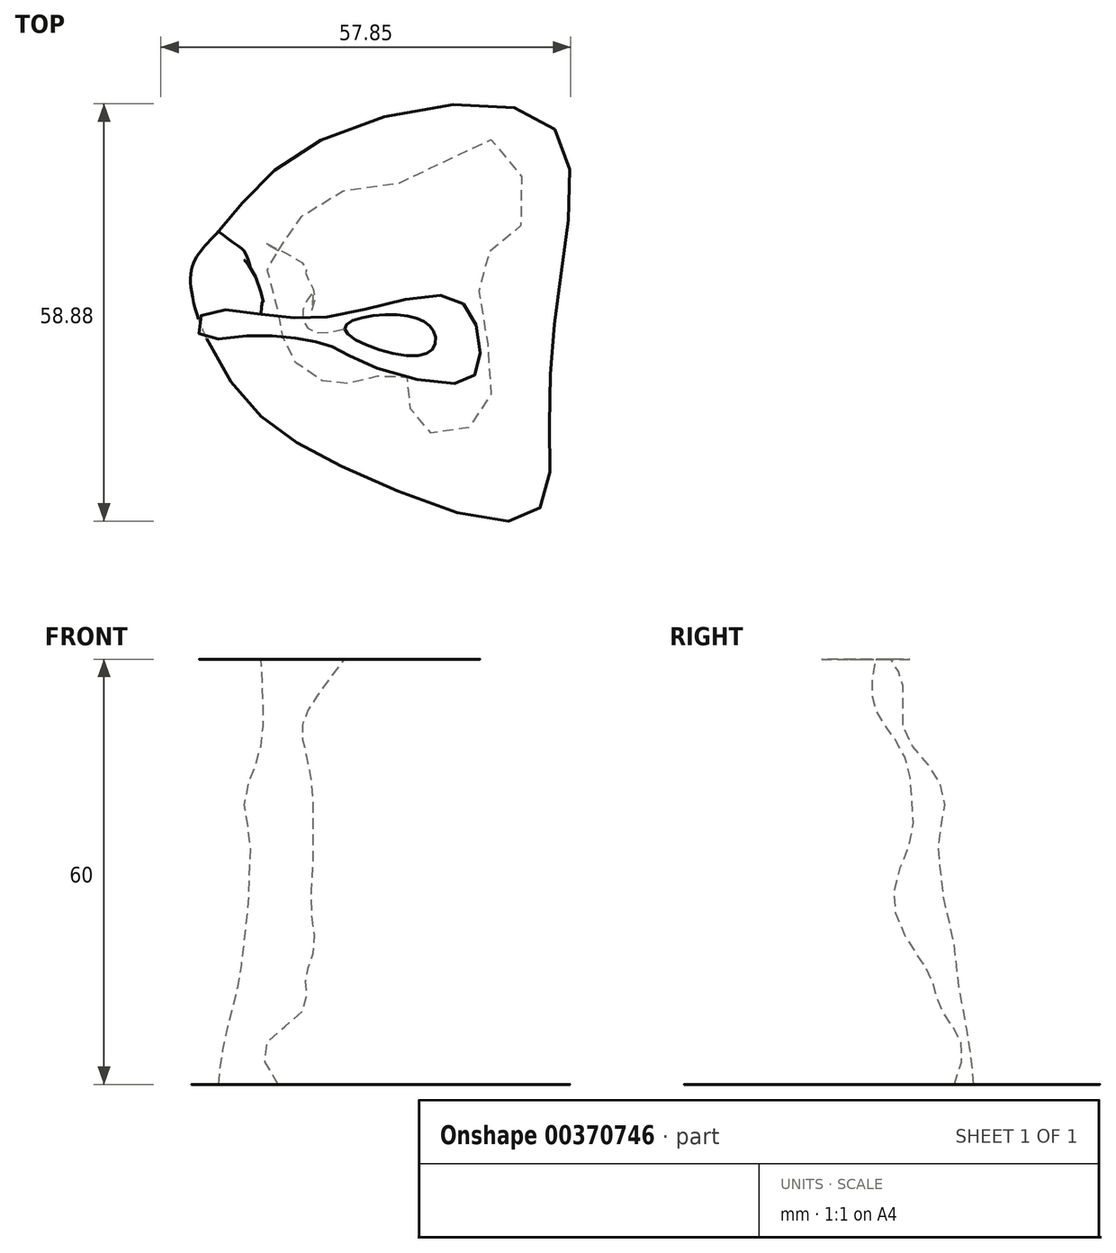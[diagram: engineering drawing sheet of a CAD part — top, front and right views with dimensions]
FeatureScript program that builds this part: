
annotation { "Feature Type Name" : "Feature", "Feature Type Description" : "" }
export const myFeature = defineFeature(function(context is Context, id is Id, definition is map)
    precondition{}
    {
        {
            var Q0;
            Q0=qCreatedBy(makeId("Top.planeOp"),FACE);
            cPlane(context, id + "F0", {"entities" : qUnion([Q0]), "cplaneType" : CPlaneType.OFFSET, "offset" : 5 * mm, "width" : 152.4 * mm, "height" : 152.4 * mm});
        }
        {
            var Q0;
            Q0=qCreatedBy(id+"F0.planeOp",FACE);
            var sketch = newSketch(context, id + "F1", { "sketchPlane" : qUnion([Q0])});
            skFitSpline(sketch, "E0", {"points": [v(-21.03, 11.8) * mm, v(-7.7, 24.1) * mm, v(25.13, 27.35) * mm, v(27.7, 8.72) * mm, v(25.64, -14.36) * mm, v(23.08, -28.38) * mm, v(-2.22, -22.05) * mm, v(-18.46, -10.6) * mm, v(-24.96, 5.81) * mm, v(-21.03, 11.8) * mm]});
            skSolve(sketch);
        }
        {
            var Q0;
            Q0=qCreatedBy(id+"F0.planeOp",FACE);
            var sketch = newSketch(context, id + "F2", { "sketchPlane" : qUnion([Q0])});
            skFitSpline(sketch, "E1", {"points": [v(-12.65, 9.06) * mm, v(-6.84, 16.24) * mm, v(7.86, 19.66) * mm, v(17.78, 24.62) * mm, v(22.22, 13.85) * mm, v(16.58, 8.2) * mm, v(16.58, -2.4) * mm, v(16.58, -13.68) * mm, v(10.09, -16.93) * mm, v(6.15, -13.85) * mm, v(5.64, -8.9) * mm, v(1.2, -8.72) * mm, v(-3.08, -9.74) * mm, v(-6.15, -9.4) * mm, v(-10.26, -6.67) * mm, v(-11.97, -3.08) * mm, v(-12.48, 0) * mm, v(-14.19, 7.35) * mm, v(-12.65, 9.06) * mm]});
            skSolve(sketch);
        }
        {
            var Q0;
            Q0=qCreatedBy(id+"F0.planeOp",FACE);
            cPlane(context, id + "F3", {"entities" : qUnion([Q0]), "cplaneType" : CPlaneType.OFFSET, "offset" : 5 * mm, "width" : 152.4 * mm, "height" : 152.4 * mm});
        }
        {
            var Q0;
            Q0=qCreatedBy(id+"F3.planeOp",FACE);
            var sketch = newSketch(context, id + "F4", { "sketchPlane" : qUnion([Q0])});
            skFitSpline(sketch, "E2", {"points": [v(-14.87, 16.93) * mm, v(-6.84, 23.6) * mm, v(6.5, 27.7) * mm, v(22.05, 28.38) * mm, v(27.18, 22.9) * mm, v(27.52, 18.12) * mm, v(25.13, 12.3) * mm, v(23.25, 8.04) * mm, v(21.88, 2.9) * mm, v(21.03, -3.25) * mm, v(22.05, -8.2) * mm, v(24.1, -13.34) * mm, v(25.13, -17.95) * mm, v(24.45, -24.1) * mm, v(21.88, -27.52) * mm, v(17.44, -27.87) * mm, v(9.57, -26.16) * mm, v(2.05, -22.9) * mm, v(-9.06, -17.27) * mm, v(-20.34, -6.5) * mm, v(-24.28, 3.76) * mm, v(-20.69, 10.94) * mm, v(-14.87, 16.93) * mm]});
            skSolve(sketch);
        }
        {
            var Q0;
            Q0=qCreatedBy(id+"F3.planeOp",FACE);
            var sketch = newSketch(context, id + "F5", { "sketchPlane" : qUnion([Q0])});
            skFitSpline(sketch, "E3", {"points": [v(-15.22, 0) * mm, v(-15.9, 7) * mm, v(-12.65, 12.82) * mm, v(-5.81, 15.56) * mm, v(9.74, 16.24) * mm, v(15.73, 20) * mm, v(17.78, 15.9) * mm, v(15.39, 10.77) * mm, v(14.87, 5.13) * mm, v(14.87, 0) * mm, v(15.39, -7) * mm, v(16.07, -12.65) * mm, v(15.73, -17.6) * mm, v(8.55, -19.66) * mm, v(5.47, -16.93) * mm, v(4.27, -13) * mm, v(1.2, -11.11) * mm, v(-5.3, -11.11) * mm, v(-11.28, -9.23) * mm, v(-12.65, -6.5) * mm, v(-15.22, 0) * mm]});
            skSolve(sketch);
        }
        {
            var Q0;
            Q0=qCreatedBy(id+"F3.planeOp",FACE);
            cPlane(context, id + "F6", {"entities" : qUnion([Q0]), "cplaneType" : CPlaneType.OFFSET, "offset" : 5 * mm, "width" : 152.4 * mm, "height" : 152.4 * mm});
        }
        {
            var Q0;
            Q0=qCreatedBy(id+"F6.planeOp",FACE);
            var sketch = newSketch(context, id + "F7", { "sketchPlane" : qUnion([Q0])});
            skFitSpline(sketch, "E4", {"points": [v(-22.9, 3.25) * mm, v(-18.98, 10.77) * mm, v(-12.82, 16.93) * mm, v(-2.56, 24.28) * mm, v(12.14, 27.35) * mm, v(22.05, 27.7) * mm, v(26.67, 21.54) * mm, v(25.3, 15.04) * mm, v(17.6, 8.38) * mm, v(15.73, 4.27) * mm, v(15.73, -3.25) * mm, v(18.12, -8.9) * mm, v(20.52, -11.8) * mm, v(21.88, -17.27) * mm, v(20.52, -21.03) * mm, v(14.7, -22.4) * mm, v(4.1, -20.69) * mm, v(-4.1, -18.12) * mm, v(-12.3, -15.04) * mm, v(-17.95, -9.06) * mm, v(-23.6, -4.79) * mm, v(-22.9, 3.25) * mm]});
            skSolve(sketch);
        }
        {
            var Q0;
            Q0=qCreatedBy(id+"F6.planeOp",FACE);
            var sketch = newSketch(context, id + "F8", { "sketchPlane" : qUnion([Q0])});
            skFitSpline(sketch, "E5", {"points": [v(-9.74, 6.84) * mm, v(-4.27, 11.28) * mm, v(6.67, 15.04) * mm, v(10.43, 12.48) * mm, v(10.26, 6.33) * mm, v(9.06, 1.88) * mm, v(8.72, -5.47) * mm, v(7.7, -8.9) * mm, v(4.96, -9.23) * mm, v(-3.93, -8.72) * mm, v(-5.81, -7) * mm, v(-7.35, -3.42) * mm, v(-8.72, 0) * mm, v(-9.74, 6.84) * mm]});
            skSolve(sketch);
        }
        {
            var Q0;
            Q0=qCreatedBy(id+"F6.planeOp",FACE);
            cPlane(context, id + "F9", {"entities" : qUnion([Q0]), "cplaneType" : CPlaneType.OFFSET, "offset" : 5 * mm, "width" : 152.4 * mm, "height" : 152.4 * mm});
        }
        {
            var Q0;
            Q0=qCreatedBy(id+"F9.planeOp",FACE);
            var sketch = newSketch(context, id + "F10", { "sketchPlane" : qUnion([Q0])});
            skFitSpline(sketch, "E6", {"points": [v(-20.34, 7) * mm, v(-13.68, 15.73) * mm, v(-5.64, 22.23) * mm, v(7.7, 26.33) * mm, v(20.86, 27.87) * mm, v(24.96, 25.47) * mm, v(26.5, 19.15) * mm, v(22.74, 14.36) * mm, v(13.16, 9.74) * mm, v(8.55, 3.08) * mm, v(10.94, -3.76) * mm, v(15.9, -9.92) * mm, v(16.75, -14.87) * mm, v(12.48, -17.44) * mm, v(3.25, -17.95) * mm, v(-6.84, -17.1) * mm, v(-14.36, -16.75) * mm, v(-22.74, -14.02) * mm, v(-27.87, -4.27) * mm, v(-24.62, 4.27) * mm, v(-20.34, 7) * mm]});
            skSolve(sketch);
        }
        {
            var Q0;
            Q0=qCreatedBy(id+"F9.planeOp",FACE);
            var sketch = newSketch(context, id + "F11", { "sketchPlane" : qUnion([Q0])});
            skFitSpline(sketch, "E7", {"points": [v(-7, 6.67) * mm, v(-4.27, 8.55) * mm, v(0, 8.9) * mm, v(2.4, 5.64) * mm, v(2.9, 0) * mm, v(2.74, -3.08) * mm, v(2.22, -8.38) * mm, v(-2.22, -9.92) * mm, v(-9.23, -9.57) * mm, v(-14.19, -8.2) * mm, v(-18.63, 0) * mm, v(-15.39, 3.42) * mm, v(-10.94, 4.96) * mm, v(-7, 6.67) * mm]});
            skSolve(sketch);
        }
        {
            var Q0;
            Q0=qCreatedBy(id+"F9.planeOp",FACE);
            cPlane(context, id + "F12", {"entities" : qUnion([Q0]), "cplaneType" : CPlaneType.OFFSET, "offset" : 5 * mm, "width" : 152.4 * mm, "height" : 152.4 * mm});
        }
        {
            var Q0;
            Q0=qCreatedBy(id+"F12.planeOp",FACE);
            var sketch = newSketch(context, id + "F13", { "sketchPlane" : qUnion([Q0])});
            skFitSpline(sketch, "E8", {"points": [v(-21.2, 5.98) * mm, v(-14.7, 12.48) * mm, v(-6.84, 20.52) * mm, v(7.18, 25.13) * mm, v(20.69, 27.35) * mm, v(26.16, 23.08) * mm, v(24.62, 17.78) * mm, v(13, 13.16) * mm, v(5.13, 8.2) * mm, v(3.6, 0) * mm, v(5.81, -3.42) * mm, v(10.6, -8.04) * mm, v(13.34, -13.16) * mm, v(3.08, -15.56) * mm, v(-17.44, -15.56) * mm, v(-25.3, -14.36) * mm, v(-28.2, -9.4) * mm, v(-28.72, -1.7) * mm, v(-25.47, 5.3) * mm, v(-21.2, 5.98) * mm]});
            skSolve(sketch);
        }
        {
            var Q0;
            Q0=qCreatedBy(id+"F12.planeOp",FACE);
            var sketch = newSketch(context, id + "F14", { "sketchPlane" : qUnion([Q0])});
            skFitSpline(sketch, "E9", {"points": [v(-16.07, 0) * mm, v(-9.57, 1.7) * mm, v(-5.3, 2.9) * mm, v(-2.9, -1.7) * mm, v(-2.9, -5.64) * mm, v(-9.74, -8.38) * mm, v(-16.93, -8.2) * mm, v(-20.52, -4.96) * mm, v(-18.46, 0) * mm, v(-16.07, 0) * mm]});
            skSolve(sketch);
        }
        {
            var Q0;
            Q0=qCreatedBy(id+"F12.planeOp",FACE);
            cPlane(context, id + "F15", {"entities" : qUnion([Q0]), "cplaneType" : CPlaneType.OFFSET, "offset" : 5 * mm, "width" : 152.4 * mm, "height" : 152.4 * mm});
        }
        {
            var Q0;
            Q0=qCreatedBy(id+"F15.planeOp",FACE);
            var sketch = newSketch(context, id + "F16", { "sketchPlane" : qUnion([Q0])});
            skFitSpline(sketch, "E10", {"points": [v(-13.5, 9.92) * mm, v(-9.74, 14.19) * mm, v(0, 20.34) * mm, v(8.55, 21.88) * mm, v(18.12, 21.88) * mm, v(19.66, 19.83) * mm, v(16.58, 18.12) * mm, v(9.23, 17.27) * mm, v(4.1, 15.22) * mm, v(2.22, 5.64) * mm, v(1.88, -1.7) * mm, v(4.27, -5.98) * mm, v(5.64, -9.57) * mm, v(2.4, -12.48) * mm, v(-7, -14.7) * mm, v(-18.8, -14.87) * mm, v(-24.28, -9.92) * mm, v(-25.47, 0) * mm, v(-22.22, 4.79) * mm, v(-16.41, 8.04) * mm, v(-13.5, 9.92) * mm]});
            skSolve(sketch);
        }
        {
            var Q0;
            Q0=qCreatedBy(id+"F15.planeOp",FACE);
            var sketch = newSketch(context, id + "F17", { "sketchPlane" : qUnion([Q0])});
            skFitSpline(sketch, "E11", {"points": [v(-16.07, -1.88) * mm, v(-12.65, 0) * mm, v(-6.84, 0) * mm, v(-6.5, -4.79) * mm, v(-10.26, -6.5) * mm, v(-14.7, -6.5) * mm, v(-16.93, -3.42) * mm, v(-16.07, -1.88) * mm]});
            skSolve(sketch);
        }
        {
            var Q0;
            Q0=qCreatedBy(id+"F15.planeOp",FACE);
            cPlane(context, id + "F18", {"entities" : qUnion([Q0]), "cplaneType" : CPlaneType.OFFSET, "offset" : 5 * mm, "width" : 152.4 * mm, "height" : 152.4 * mm});
        }
        {
            var Q0;
            Q0=qCreatedBy(id+"F18.planeOp",FACE);
            var sketch = newSketch(context, id + "F19", { "sketchPlane" : qUnion([Q0])});
            skFitSpline(sketch, "E12", {"points": [v(-11.97, 9.06) * mm, v(-6.67, 13.5) * mm, v(0, 18.3) * mm, v(3.42, 17.1) * mm, v(4.96, 13.34) * mm, v(5.98, 3.42) * mm, v(4.96, -3.42) * mm, v(3.76, -9.92) * mm, v(0, -11.97) * mm, v(-10.43, -13.85) * mm, v(-19.83, -14.02) * mm, v(-25.3, -11.28) * mm, v(-27.01, -3.25) * mm, v(-24.62, 3.93) * mm, v(-17.1, 7) * mm, v(-11.97, 9.06) * mm]});
            skSolve(sketch);
        }
        {
            var Q0;
            Q0=qCreatedBy(id+"F18.planeOp",FACE);
            var sketch = newSketch(context, id + "F20", { "sketchPlane" : qUnion([Q0])});
            skFitSpline(sketch, "E13", {"points": [v(-13.16, -4.62) * mm, v(-19.32, -3.6) * mm, v(-17.78, 0) * mm, v(-10.09, 1.54) * mm, v(-6.33, 0) * mm, v(-6.67, -5.64) * mm, v(-13.16, -4.62) * mm]});
            skSolve(sketch);
        }
        {
            var Q0;
            Q0=qCreatedBy(id+"F18.planeOp",FACE);
            cPlane(context, id + "F21", {"entities" : qUnion([Q0]), "cplaneType" : CPlaneType.OFFSET, "offset" : 5 * mm, "width" : 152.4 * mm, "height" : 152.4 * mm});
        }
        {
            var Q0;
            Q0=qCreatedBy(id+"F21.planeOp",FACE);
            var sketch = newSketch(context, id + "F22", { "sketchPlane" : qUnion([Q0])});
            skFitSpline(sketch, "E14", {"points": [v(-10.43, 7.7) * mm, v(-4.27, 13.5) * mm, v(3.08, 18.46) * mm, v(12.14, 18.63) * mm, v(13.85, 13.68) * mm, v(12.3, 9.4) * mm, v(11.11, 4.62) * mm, v(11.28, -1.37) * mm, v(9.74, -7.35) * mm, v(10.43, -13.68) * mm, v(6.5, -17.44) * mm, v(0, -18.63) * mm, v(-10.6, -19.32) * mm, v(-22.22, -13) * mm, v(-26.33, -2.22) * mm, v(-24.96, 3.08) * mm, v(-18.63, 6.67) * mm, v(-10.43, 7.7) * mm]});
            skSolve(sketch);
        }
        {
            var Q0;
            Q0=qCreatedBy(id+"F21.planeOp",FACE);
            var sketch = newSketch(context, id + "F23", { "sketchPlane" : qUnion([Q0])});
            skFitSpline(sketch, "E15", {"points": [v(-16.07, 0) * mm, v(-14.36, 1.88) * mm, v(-5.98, 2.74) * mm, v(-5.13, 0) * mm, v(-7.35, -5.81) * mm, v(-13, -6.84) * mm, v(-16.07, 0) * mm]});
            skSolve(sketch);
        }
        {
            var Q0;
            Q0=qCreatedBy(id+"F21.planeOp",FACE);
            cPlane(context, id + "F24", {"entities" : qUnion([Q0]), "cplaneType" : CPlaneType.OFFSET, "offset" : 5 * mm, "width" : 152.4 * mm, "height" : 152.4 * mm});
        }
        {
            var Q0;
            Q0=qCreatedBy(id+"F24.planeOp",FACE);
            var sketch = newSketch(context, id + "F25", { "sketchPlane" : qUnion([Q0])});
            skFitSpline(sketch, "E16", {"points": [v(-16.75, 8.2) * mm, v(-6.84, 13.85) * mm, v(0, 19.15) * mm, v(17.27, 20.69) * mm, v(21.2, 14.36) * mm, v(21.71, 6.5) * mm, v(21.37, 0) * mm, v(13.85, -13) * mm, v(3.42, -16.24) * mm, v(-12.82, -14.53) * mm, v(-24.45, -10.94) * mm, v(-27.18, 1.54) * mm, v(-19.49, 5.98) * mm, v(-16.75, 8.2) * mm]});
            skSolve(sketch);
        }
        {
            var Q0;
            Q0=qCreatedBy(id+"F24.planeOp",FACE);
            var sketch = newSketch(context, id + "F26", { "sketchPlane" : qUnion([Q0])});
            skFitSpline(sketch, "E17", {"points": [v(-10.94, -3.6) * mm, v(-19.83, -1.7) * mm, v(-17.78, 3.42) * mm, v(-8.38, 3.6) * mm, v(-5.13, -1.88) * mm, v(-10.94, -3.6) * mm]});
            skSolve(sketch);
        }
        {
            var Q0;
            Q0=qCreatedBy(id+"F24.planeOp",FACE);
            cPlane(context, id + "F27", {"entities" : qUnion([Q0]), "cplaneType" : CPlaneType.OFFSET, "offset" : 5 * mm, "width" : 152.4 * mm, "height" : 152.4 * mm});
        }
        {
            var Q0;
            Q0=qCreatedBy(id+"F27.planeOp",FACE);
            var sketch = newSketch(context, id + "F28", { "sketchPlane" : qUnion([Q0])});
            skFitSpline(sketch, "E18", {"points": [v(-22.22, 1.54) * mm, v(-14.19, 6.5) * mm, v(-9.92, 8.72) * mm, v(-3.42, 13.34) * mm, v(5.3, 15.56) * mm, v(13.85, 16.58) * mm, v(20.52, 13) * mm, v(24.1, 4.1) * mm, v(23.6, -4.27) * mm, v(22.9, -9.06) * mm, v(19.49, -14.53) * mm, v(15.22, -16.07) * mm, v(5.98, -16.07) * mm, v(-4.1, -13.5) * mm, v(-8.2, -11.97) * mm, v(-16.24, -10.43) * mm, v(-21.71, -9.57) * mm, v(-24.45, -8.72) * mm, v(-27.35, -6.84) * mm, v(-26.16, 0) * mm, v(-22.22, 1.54) * mm]});
            skSolve(sketch);
        }
        {
            var Q0;
            Q0=qCreatedBy(id+"F27.planeOp",FACE);
            var sketch = newSketch(context, id + "F29", { "sketchPlane" : qUnion([Q0])});
            skFitSpline(sketch, "E19", {"points": [v(-17.27, 0) * mm, v(-10.26, 3.42) * mm, v(-6.67, 0) * mm, v(-4.27, -5.98) * mm, v(-10.26, -4.45) * mm, v(-14.36, -4.27) * mm, v(-17.27, 0) * mm]});
            skSolve(sketch);
        }
        {
            var Q0;
            Q0=qCreatedBy(id+"F27.planeOp",FACE);
            cPlane(context, id + "F30", {"entities" : qUnion([Q0]), "cplaneType" : CPlaneType.OFFSET, "offset" : 5 * mm, "width" : 152.4 * mm, "height" : 152.4 * mm});
        }
        {
            var Q0;
            Q0=qCreatedBy(id+"F30.planeOp",FACE);
            var sketch = newSketch(context, id + "F31", { "sketchPlane" : qUnion([Q0])});
            skFitSpline(sketch, "E20", {"points": [v(-18.63, 1.54) * mm, v(-14.87, 1.88) * mm, v(-8.04, 5.13) * mm, v(-1.88, 8.55) * mm, v(4.96, 11.63) * mm, v(10.94, 11.63) * mm, v(22.4, 7.52) * mm, v(23.42, 3.25) * mm, v(25.13, -9.06) * mm, v(23.42, -15.04) * mm, v(19.32, -18.12) * mm, v(13.68, -19.66) * mm, v(9.4, -19.32) * mm, v(4.96, -17.27) * mm, v(2.9, -13.85) * mm, v(-3.93, -10.77) * mm, v(-6.5, -9.92) * mm, v(-10.26, -8.72) * mm, v(-14.87, -8.04) * mm, v(-17.44, -8.2) * mm, v(-21.54, -8.9) * mm, v(-28.04, -7.52) * mm, v(-27.52, -4.27) * mm, v(-25.3, 0) * mm, v(-18.63, 1.54) * mm]});
            skSolve(sketch);
        }
        {
            var Q0;
            Q0=qCreatedBy(id+"F30.planeOp",FACE);
            var sketch = newSketch(context, id + "F32", { "sketchPlane" : qUnion([Q0])});
            skFitSpline(sketch, "E21", {"points": [v(-16.75, -1.37) * mm, v(-10.43, 0) * mm, v(-5.98, -1.88) * mm, v(2.05, -3.25) * mm, v(6.84, -8.04) * mm, v(1.37, -7.7) * mm, v(-4.79, -4.27) * mm, v(-12.3, -2.22) * mm, v(-16.75, -1.37) * mm]});
            skSolve(sketch);
        }
        {
            var Q0;
            Q0=qCreatedBy(id+"F30.planeOp",FACE);
            cPlane(context, id + "F33", {"entities" : qUnion([Q0]), "cplaneType" : CPlaneType.OFFSET, "offset" : 5 * mm, "width" : 152.4 * mm, "height" : 152.4 * mm});
        }
        {
            var Q0;
            Q0=qCreatedBy(id+"F33.planeOp",FACE);
            var sketch = newSketch(context, id + "F34", { "sketchPlane" : qUnion([Q0])});
            skFitSpline(sketch, "E22", {"points": [v(-25.64, 0) * mm, v(-5.3, 3.6) * mm, v(1.37, 8.04) * mm, v(12.65, 9.23) * mm, v(19.83, 7) * mm, v(22.9, 0) * mm, v(24.79, -14.87) * mm, v(22.4, -22.9) * mm, v(11.8, -24.79) * mm, v(9.23, -23.76) * mm, v(5.64, -20.17) * mm, v(-2.05, -8.55) * mm, v(-12.14, -6.84) * mm, v(-23.6, -6.5) * mm, v(-26.84, -2.9) * mm, v(-25.64, 0) * mm]});
            skSolve(sketch);
        }
        {
            var Q0;
            Q0=qCreatedBy(id+"F33.planeOp",FACE);
            var sketch = newSketch(context, id + "F35", { "sketchPlane" : qUnion([Q0])});
            skFitSpline(sketch, "E23", {"points": [v(-5.3, -1.54) * mm, v(6.33, -2.56) * mm, v(11.11, -4.79) * mm, v(13.5, -9.57) * mm, v(6.84, -9.74) * mm, v(0, -6.5) * mm, v(-7.52, -4.27) * mm, v(-5.3, -1.54) * mm]});
            skSolve(sketch);
        }
        {
            var Q0;
            Q0=qCreatedBy(id+"F33.planeOp",FACE);
            cPlane(context, id + "F36", {"entities" : qUnion([Q0]), "cplaneType" : CPlaneType.OFFSET, "offset" : 5 * mm, "width" : 152.4 * mm, "height" : 152.4 * mm});
        }
        {
            var Q0;
            Q0=qCreatedBy(id+"F36.planeOp",FACE);
            var sketch = newSketch(context, id + "F37", { "sketchPlane" : qUnion([Q0])});
            skFitSpline(sketch, "E24", {"points": [v(-23.42, 0) * mm, v(-14.53, 0) * mm, v(-3.76, 0) * mm, v(10.26, 2.74) * mm, v(14.7, 0) * mm, v(15.73, -6.84) * mm, v(13.34, -9.57) * mm, v(0, -7) * mm, v(-4.79, -4.62) * mm, v(-7.52, -3.76) * mm, v(-11.8, -3.08) * mm, v(-17.95, -3.08) * mm, v(-23.6, -2.9) * mm, v(-23.42, 0) * mm]});
            skSolve(sketch);
        }
        {
            var Q0;
            Q0=qCreatedBy(id+"F36.planeOp",FACE);
            var sketch = newSketch(context, id + "F38", { "sketchPlane" : qUnion([Q0])});
            skFitSpline(sketch, "E25", {"points": [v(-3.25, -2.05) * mm, v(4.27, 0) * mm, v(9.4, -2.56) * mm, v(7.86, -5.64) * mm, v(-3.25, -2.05) * mm]});
            skSolve(sketch);
        }
        {
            var Q0;
            Q0 = qSketchRegion(id + "F1", true);
            var Q1;
            Q1 = qSketchRegion(id + "F4", true);
            var Q2;
            Q2 = qSketchRegion(id + "F7", true);
            var Q3;
            Q3 = qSketchRegion(id + "F10", true);
            var Q4;
            Q4 = qSketchRegion(id + "F13", true);
            var Q5;
            Q5 = qSketchRegion(id + "F16", true);
            var Q6;
            Q6 = qSketchRegion(id + "F19", true);
            var Q7;
            Q7 = qSketchRegion(id + "F22", true);
            var Q8;
            Q8 = qSketchRegion(id + "F25", true);
            var Q9;
            Q9 = qSketchRegion(id + "F28", true);
            var Q10;
            Q10 = qSketchRegion(id + "F31", true);
            var Q11;
            Q11 = qSketchRegion(id + "F34", true);
            var Q12;
            Q12 = qSketchRegion(id + "F37", true);
            loft(context, id + "F39", {"sheetProfilesArray" : [{ "sheetProfileEntities" : qUnion([Q0]) }, { "sheetProfileEntities" : qUnion([Q1]) }, { "sheetProfileEntities" : qUnion([Q2]) }, { "sheetProfileEntities" : qUnion([Q3]) }, { "sheetProfileEntities" : qUnion([Q4]) }, { "sheetProfileEntities" : qUnion([Q5]) }, { "sheetProfileEntities" : qUnion([Q6]) }, { "sheetProfileEntities" : qUnion([Q7]) }, { "sheetProfileEntities" : qUnion([Q8]) }, { "sheetProfileEntities" : qUnion([Q9]) }, { "sheetProfileEntities" : qUnion([Q10]) }, { "sheetProfileEntities" : qUnion([Q11]) }, { "sheetProfileEntities" : qUnion([Q12]) }]});
        }
        {
            var Q1;
            Q1 = qSketchRegion(id + "F2", true);
            var Q2;
            Q2 = qSketchRegion(id + "F5", true);
            var Q3;
            Q3 = qSketchRegion(id + "F8", true);
            var Q4;
            Q4 = qSketchRegion(id + "F11", true);
            var Q5;
            Q5 = qSketchRegion(id + "F14", true);
            var Q6;
            Q6 = qSketchRegion(id + "F17", true);
            var Q7;
            Q7 = qSketchRegion(id + "F20", true);
            var Q8;
            Q8 = qSketchRegion(id + "F23", true);
            var Q9;
            Q9 = qSketchRegion(id + "F26", true);
            var Q10;
            Q10 = qSketchRegion(id + "F29", true);
            var Q11;
            Q11 = qSketchRegion(id + "F32", true);
            var Q12;
            Q12 = qSketchRegion(id + "F35", true);
            var Q13;
            Q13 = qSketchRegion(id + "F38", true);
            loft(context, id + "F40", {"operationType" : NewBodyOperationType.REMOVE, "sheetProfilesArray" : [{ "sheetProfileEntities" : qUnion([Q1]) }, { "sheetProfileEntities" : qUnion([Q2]) }, { "sheetProfileEntities" : qUnion([Q3]) }, { "sheetProfileEntities" : qUnion([Q4]) }, { "sheetProfileEntities" : qUnion([Q5]) }, { "sheetProfileEntities" : qUnion([Q6]) }, { "sheetProfileEntities" : qUnion([Q7]) }, { "sheetProfileEntities" : qUnion([Q8]) }, { "sheetProfileEntities" : qUnion([Q9]) }, { "sheetProfileEntities" : qUnion([Q10]) }, { "sheetProfileEntities" : qUnion([Q11]) }, { "sheetProfileEntities" : qUnion([Q12]) }, { "sheetProfileEntities" : qUnion([Q13]) }]});
        }
    });
